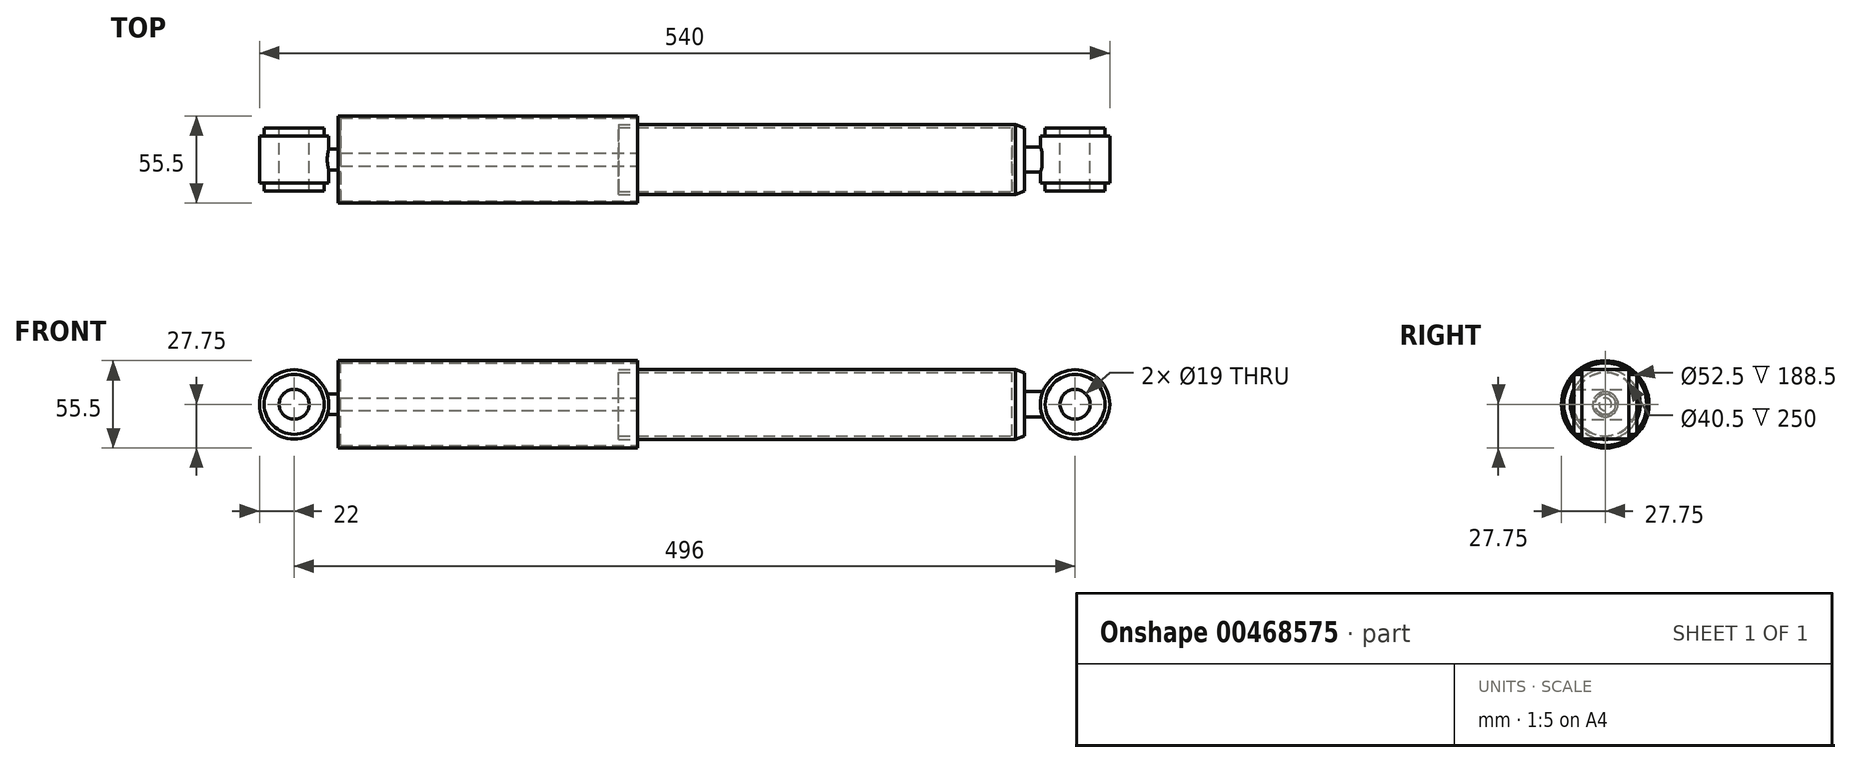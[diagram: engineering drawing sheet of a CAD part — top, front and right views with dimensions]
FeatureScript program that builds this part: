
annotation { "Feature Type Name" : "Feature", "Feature Type Description" : "" }
export const myFeature = defineFeature(function(context is Context, id is Id, definition is map)
    precondition{}
    {
        {
            var Q0;
            Q0=qCreatedBy(makeId("Front.planeOp"),FACE);
            var sketch = newSketch(context, id + "F0", { "sketchPlane" : qUnion([Q0])});
            skLineSegment(sketch, "E0", {"start": v(0, 0) * mm, "end": v(496, 0) * mm, "construction": true});
            skCircle(sketch, "E1", {"center": v(0, 0) * mm, "radius": 22 * mm});
            skPoint(sketch, "E2", {"position": v(218, 0) * mm});
            skLineSegment(sketch, "E3", {"start": v(218, 0) * mm, "end": v(218, 27.75) * mm});
            skLineSegment(sketch, "E4", {"start": v(218, 27.75) * mm, "end": v(28, 27.75) * mm});
            skLineSegment(sketch, "E5", {"start": v(28, 27.75) * mm, "end": v(28, 0) * mm});
            skLineSegment(sketch, "E6", {"start": v(28, 0) * mm, "end": v(29.5, 0) * mm});
            skLineSegment(sketch, "E7", {"start": v(29.5, 0) * mm, "end": v(29.5, 26.25) * mm});
            skLineSegment(sketch, "E8", {"start": v(29.5, 26.25) * mm, "end": v(218, 26.25) * mm});
            skPoint(sketch, "E9", {"position": v(458, 0) * mm});
            skLineSegment(sketch, "E10", {"start": v(458, 0) * mm, "end": v(458, 22.25) * mm});
            skLineSegment(sketch, "E11", {"start": v(458, 22.25) * mm, "end": v(206, 22.25) * mm});
            skLineSegment(sketch, "E12", {"start": v(206, 22.25) * mm, "end": v(206, 20.25) * mm});
            skLineSegment(sketch, "E13", {"start": v(206, 20.25) * mm, "end": v(456, 20.25) * mm});
            skLineSegment(sketch, "E14", {"start": v(456, 20.25) * mm, "end": v(456, 0) * mm});
            skLineSegment(sketch, "E15", {"start": v(456, 0) * mm, "end": v(458, 0) * mm});
            skLineSegment(sketch, "E16", {"start": v(29.5, 4) * mm, "end": v(456, 4) * mm});
            skLineSegment(sketch, "E17", {"start": v(456, 4) * mm, "end": v(456, 0) * mm});
            skLineSegment(sketch, "E18", {"start": v(456, 0) * mm, "end": v(29.5, 0) * mm});
            skLineSegment(sketch, "E19", {"start": v(28, 0) * mm, "end": v(22, 0) * mm});
            skPoint(sketch, "E20", {"position": v(21, 0) * mm});
            skLineSegment(sketch, "E21", {"start": v(21, 0) * mm, "end": v(21, 6.56) * mm});
            skLineSegment(sketch, "E22", {"start": v(21, 6.56) * mm, "end": v(28, 6.56) * mm});
            skCircle(sketch, "E23", {"center": v(496, 0) * mm, "radius": 22 * mm});
            skLineSegment(sketch, "E24", {"start": v(458, 0) * mm, "end": v(464, 0) * mm});
            skLineSegment(sketch, "E25", {"start": v(464, 0) * mm, "end": v(464, 20) * mm});
            skLineSegment(sketch, "E26", {"start": v(464, 20) * mm, "end": v(458, 22.25) * mm});
            skLineSegment(sketch, "E27", {"start": v(464, 0) * mm, "end": v(474, 0) * mm});
            skLineSegment(sketch, "E28", {"start": v(475, 0) * mm, "end": v(464, 0) * mm});
            skLineSegment(sketch, "E29", {"start": v(475, 0) * mm, "end": v(475, 8) * mm});
            skLineSegment(sketch, "E30", {"start": v(475, 8) * mm, "end": v(464, 8) * mm});
            skSolve(sketch);
        }
        {
            var Q0;
            {var subQ3=sQuery(id+"F0.wireOp",EDGE,"E4");Q0=makeQuery(id+"F0.imprint","IMPRINT",FACE,{"disambiguationData":[TD([[makeQuery(id+"F0.imprint","IMPRINT",EDGE,{"derivedFrom":subQ3}),1.0]])]});}
            var Q1;
            {var subQ0=sQuery(id+"F0.wireOp",EDGE,"E19");Q1=makeQuery(id+"F0.imprint","IMPRINT",FACE,{"disambiguationData":[TD([[makeQuery(id+"F0.imprint","IMPRINT",EDGE,{"derivedFrom":subQ0}),-1.0]])]});}
            var Q2;
            {var subQ0=sQuery(id+"F0.wireOp",EDGE,"E18");var subQ1=sQuery(id+"F0.wireOp",EDGE,"E3");var subQ2=makeQuery(id+"F0.imprint","INTERSECT",VERTEX,{"derivedFrom":[subQ1,subQ0]});Q2=makeQuery(id+"F0.imprint","IMPRINT",FACE,{"disambiguationData":[TD([[makeQuery(id+"F0.imprint","IMPRINT",EDGE,{"disambiguationData":[TD([[subQ2,-1.0]])],"derivedFrom":subQ1}),1.0]])]});}
            var Q3;
            {var subQ1=sQuery(id+"F0.wireOp",EDGE,"E10");Q3=makeQuery(id+"F0.imprint","IMPRINT",FACE,{"disambiguationData":[TD([[makeQuery(id+"F0.imprint","IMPRINT",EDGE,{"derivedFrom":subQ1}),1.0]])]});}
            var Q4;
            {var subQ5=sQuery(id+"F0.wireOp",EDGE,"E12");Q4=makeQuery(id+"F0.imprint","IMPRINT",FACE,{"disambiguationData":[TD([[makeQuery(id+"F0.imprint","IMPRINT",EDGE,{"derivedFrom":subQ5}),1.0]])]});}
            var Q5;
            {var subQ5=sQuery(id+"F0.wireOp",EDGE,"E17");Q5=makeQuery(id+"F0.imprint","IMPRINT",FACE,{"disambiguationData":[TD([[makeQuery(id+"F0.imprint","IMPRINT",EDGE,{"derivedFrom":subQ5}),-1.0]])]});}
            var Q6;
            Q6=makeQuery(id+"F0.imprint","IMPRINT",FACE,{"disambiguationData":[TD([[makeQuery(id+"F0.imprint","IMPRINT",EDGE,{"derivedFrom":sQuery(id+"F0.wireOp",EDGE,"E10")}),-1.0]])]});
            var Q7;
            {var subQ0=sQuery(id+"F0.wireOp",EDGE,"E30");Q7=makeQuery(id+"F0.imprint","IMPRINT",FACE,{"disambiguationData":[TD([[makeQuery(id+"F0.imprint","IMPRINT",EDGE,{"derivedFrom":subQ0}),1.0]])]});}
            var Q8;
            {var subQ0=sQuery(id+"F0.wireOp",EDGE,"E28");var subQ1=sQuery(id+"F0.wireOp",EDGE,"E23");var subQ2=makeQuery(id+"F0.imprint","INTERSECT",VERTEX,{"derivedFrom":[subQ1,subQ0]});Q8=makeQuery(id+"F0.imprint","IMPRINT",FACE,{"disambiguationData":[TD([[makeQuery(id+"F0.imprint","IMPRINT",EDGE,{"disambiguationData":[TD([[subQ2,1.0]])],"derivedFrom":subQ1}),1.0]])]});}
            var Q9;
            Q9=sQuery(id+"F0.wireOp",EDGE,"E18");
            revolve(context, id + "F1", {"surfaceOperationType" : NewSurfaceOperationType.NEW, "entities" : qUnion([Q0, Q1, Q2, Q3, Q4, Q5, Q6, Q7, Q8]), "axis" : qUnion([Q9]), "revolveType" : RevolveType.FULL});
        }
        {
            var Q0;
            Q0=qCreatedBy(makeId("Front.planeOp"),FACE);
            var sketch = newSketch(context, id + "F2", { "sketchPlane" : qUnion([Q0])});
            skCircle(sketch, "E31", {"center": v(0, 0) * mm, "radius": 22 * mm});
            skCircle(sketch, "E32", {"center": v(0, 0) * mm, "radius": 19 * mm});
            skLineSegment(sketch, "E33.0", {"start": v(475, 8) * mm, "end": v(475, -8) * mm});
            skPoint(sketch, "E34", {"position": v(496, 0) * mm});
            skPoint(sketch, "E34.positionSnap0", {"position": v(475, 0) * mm});
            skCircle(sketch, "E35", {"center": v(496, 0) * mm, "radius": 22 * mm});
            skCircle(sketch, "E36", {"center": v(496, 0) * mm, "radius": 19 * mm});
            skSolve(sketch);
        }
        {
            var Q0;
            Q0 = qSketchRegion(id + "F2", true);
            extrude(context, id + "F3", {"entities" : qUnion([Q0]), "operationType" : NewBodyOperationType.ADD, "depth" : 30 * mm, "offsetDistance" : 25 * mm, "symmetric" : true});
        }
        {
            var Q0;
            Q0=qCreatedBy(makeId("Front.planeOp"),FACE);
            var sketch = newSketch(context, id + "F4", { "sketchPlane" : qUnion([Q0])});
            skCircle(sketch, "E37.0", {"center": v(0, 0) * mm, "radius": 19 * mm});
            skCircle(sketch, "E38.0", {"center": v(496, 0) * mm, "radius": 19 * mm});
            skCircle(sketch, "E39", {"center": v(0, 0) * mm, "radius": 9.5 * mm});
            skCircle(sketch, "E40", {"center": v(496, 0) * mm, "radius": 9.5 * mm});
            skSolve(sketch);
        }
        {
            var Q0;
            Q0 = qSketchRegion(id + "F4", true);
            extrude(context, id + "F5", {"entities" : qUnion([Q0]), "operationType" : NewBodyOperationType.ADD, "depth" : 40 * mm, "offsetDistance" : 25 * mm, "symmetric" : true});
        }
    });
